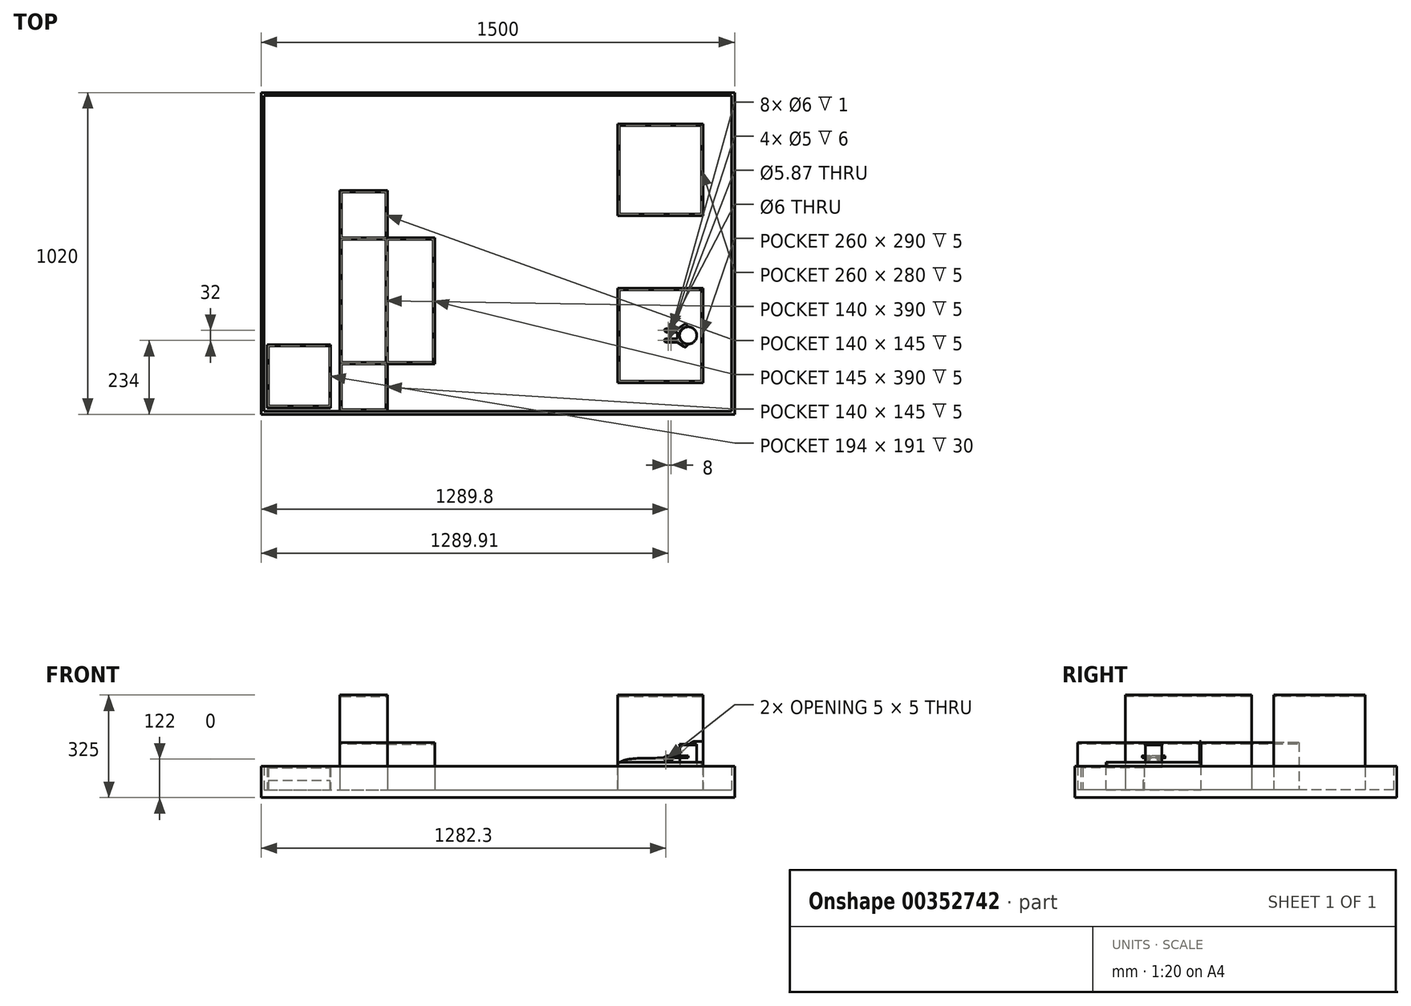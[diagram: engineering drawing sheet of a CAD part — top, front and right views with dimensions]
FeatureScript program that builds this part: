
annotation { "Feature Type Name" : "Feature", "Feature Type Description" : "" }
export const myFeature = defineFeature(function(context is Context, id is Id, definition is map)
    precondition{}
    {
        {
            var Q0;
            Q0=qCreatedBy(makeId("Top.planeOp"),FACE);
            var sketch = newSketch(context, id + "F0", { "sketchPlane" : qUnion([Q0])});
            skCircle(sketch, "E0", {"center": v(0, 0) * mm, "radius": 27.2 * mm});
            skSolve(sketch);
        }
        {
            var Q0;
            Q0=qSketchRegion(id+"F0",true);
            extrude(context, id + "F1", {"entities" : qUnion([Q0]), "depth" : 2.83 * mm});
        }
        {
            var Q0;
            Q0=makeQuery(id+"F1.opExtrude","CAP_FACE",FACE,{"disambiguationData":[OSD([sQuery(id+"F0.wireOp",EDGE,"E0")])],"isStart":false});
            var sketch = newSketch(context, id + "F2", { "sketchPlane" : qUnion([Q0])});
            skCircle(sketch, "E1", {"center": v(0, 0) * mm, "radius": 26.4 * mm});
            skSolve(sketch);
        }
        {
            var Q0;
            Q0=qSketchRegion(id+"F2",true);
            extrude(context, id + "F3", {"entities" : qUnion([Q0]), "operationType" : NewBodyOperationType.ADD, "depth" : 67.36 * mm});
        }
        {
            var Q0;
            Q0=makeQuery(id+"F3.opExtrude","CAP_FACE",FACE,{"disambiguationData":[OSD([sQuery(id+"F2.wireOp",EDGE,"E1")])],"isStart":false});
            var sketch = newSketch(context, id + "F4", { "sketchPlane" : qUnion([Q0])});
            skCircle(sketch, "E2", {"center": v(0, 0) * mm, "radius": 27.2 * mm});
            skSolve(sketch);
        }
        {
            var Q0;
            Q0=qSketchRegion(id+"F4",true);
            extrude(context, id + "F5", {"entities" : qUnion([Q0]), "operationType" : NewBodyOperationType.ADD, "depth" : 2.83 * mm});
        }
        {
            var Q0;
            Q0=makeQuery(id+"F5.opExtrude","CAP_FACE",FACE,{"disambiguationData":[OSD([sQuery(id+"F4.wireOp",EDGE,"E2")])],"isStart":false});
            var sketch = newSketch(context, id + "F6", { "sketchPlane" : qUnion([Q0])});
            skSolve(sketch);
        }
        {
            var Q0;
            Q0=qCreatedBy(makeId("Top.planeOp"),FACE);
            cPlane(context, id + "F7", {"entities" : qUnion([Q0]), "cplaneType" : CPlaneType.OFFSET, "offset" : 25 * mm, "width" : 150 * mm, "height" : 150 * mm});
        }
        {
            var Q0;
            Q0=makeQuery(id+"F6.imprint","IMPRINT",FACE,{"disambiguationData":[TD([[makeQuery(id+"F6.imprint","IMPRINT",EDGE,{"derivedFrom":makeQuery(id+"F5.opExtrude","CAP_EDGE",EDGE,{"disambiguationData":[OSD([sQuery(id+"F4.wireOp",EDGE,"E2")])],"isStart":false})}),1.0]])]});
            var sketch = newSketch(context, id + "F8", { "sketchPlane" : qUnion([Q0])});
            skSolve(sketch);
        }
        {
            var Q0;
            Q0=qCreatedBy(makeId("Top.planeOp"),FACE);
            var sketch = newSketch(context, id + "F9", { "sketchPlane" : qUnion([Q0])});
            skLineSegment(sketch, "E3.bottom", {"start": v(-222.8, -150) * mm, "end": v(47.2, -150) * mm});
            skLineSegment(sketch, "E3.top", {"start": v(-222.8, 150) * mm, "end": v(47.2, 150) * mm});
            skLineSegment(sketch, "E3.left", {"start": v(-222.8, -150) * mm, "end": v(-222.8, 150) * mm});
            skLineSegment(sketch, "E3.right", {"start": v(47.2, -150) * mm, "end": v(47.2, 150) * mm});
            skSolve(sketch);
        }
        {
            var Q0;
            Q0=qSketchRegion(id+"F9",true);
            extrude(context, id + "F10", {"entities" : qUnion([Q0]), "oppositeDirection" : true, "depth" : 72 * mm});
        }
        {
            var Q0;
            Q0=makeQuery(id+"F10.opExtrude","CAP_FACE",FACE,{"disambiguationData":[OSD([sQuery(id+"F9.wireOp",EDGE,"E3.bottom"),sQuery(id+"F9.wireOp",EDGE,"E3.top"),sQuery(id+"F9.wireOp",EDGE,"E3.left"),sQuery(id+"F9.wireOp",EDGE,"E3.right")])],"isStart":true});
            var sketch = newSketch(context, id + "F11", { "sketchPlane" : qUnion([Q0])});
            skLineSegment(sketch, "E4.bottom", {"start": v(-222.8, -150) * mm, "end": v(47.2, -150) * mm});
            skLineSegment(sketch, "E4.top", {"start": v(-222.8, -145) * mm, "end": v(42.2, -145) * mm});
            skLineSegment(sketch, "E4.left", {"start": v(-222.8, -150) * mm, "end": v(-222.8, -145) * mm});
            skLineSegment(sketch, "E5.bottom", {"start": v(47.2, 150) * mm, "end": v(42.2, 150) * mm});
            skLineSegment(sketch, "E5.left", {"start": v(47.2, 150) * mm, "end": v(47.2, -150) * mm});
            skLineSegment(sketch, "E5.right", {"start": v(42.2, 150) * mm, "end": v(42.2, -145) * mm});
            skSolve(sketch);
        }
        {
            var Q0;
            Q0=qSketchRegion(id+"F11",true);
            extrude(context, id + "F12", {"entities" : qUnion([Q0]), "operationType" : NewBodyOperationType.ADD, "depth" : 15 * mm});
        }
        {
            var Q0;
            Q0=makeQuery(id+"F12.boolean.opBoolean","MERGE",FACE,{"derivedFrom":[makeQuery(id+"F10.opExtrude","SWEPT_FACE",FACE,{"disambiguationData":[OSD([sQuery(id+"F9.wireOp",EDGE,"E3.top")])]}),makeQuery(id+"F12.opExtrude","SWEPT_FACE",FACE,{"disambiguationData":[OSD([sQuery(id+"F11.wireOp",EDGE,"E5.bottom")])]})]});
            var sketch = newSketch(context, id + "F13", { "sketchPlane" : qUnion([Q0])});
            skLineSegment(sketch, "E6", {"start": v(-47.2, 81.36) * mm, "end": v(-21.31, 81.36) * mm});
            skFitSpline(sketch, "E7", {"points": [v(-21.31, 81.36) * mm, v(15.24, 52.01) * mm, v(114.14, 28.17) * mm, v(222.8, 0) * mm], "startDerivative": vector(181.02, 0.3) * mm, "endDerivative": vector(-1.73, -239.85) * mm});
            skLineSegment(sketch, "E8", {"start": v(-47.2, 81.36) * mm, "end": v(-47.2, -72) * mm});
            skLineSegment(sketch, "E9", {"start": v(-47.2, -72) * mm, "end": v(222.8, -72) * mm});
            skLineSegment(sketch, "E10", {"start": v(222.8, -72) * mm, "end": v(222.8, 0) * mm});
            skSolve(sketch);
        }
        {
            var Q0;
            Q0=qSketchRegion(id+"F13",true);
            extrude(context, id + "F14", {"entities" : qUnion([Q0]), "operationType" : NewBodyOperationType.ADD, "oppositeDirection" : true, "depth" : 5 * mm});
        }
        {
            var Q0;
            Q0=makeQuery(id+"F10.opExtrude","CAP_FACE",FACE,{"disambiguationData":[OSD([sQuery(id+"F9.wireOp",EDGE,"E3.bottom"),sQuery(id+"F9.wireOp",EDGE,"E3.top"),sQuery(id+"F9.wireOp",EDGE,"E3.left"),sQuery(id+"F9.wireOp",EDGE,"E3.right")])],"isStart":true});
            var sketch = newSketch(context, id + "F15", { "sketchPlane" : qUnion([Q0])});
            skLineSegment(sketch, "E11.bottom", {"start": v(-222.8, 145) * mm, "end": v(-217.8, 145) * mm});
            skLineSegment(sketch, "E11.top", {"start": v(-222.8, -145) * mm, "end": v(-217.8, -145) * mm});
            skLineSegment(sketch, "E11.left", {"start": v(-222.8, 145) * mm, "end": v(-222.8, -145) * mm});
            skLineSegment(sketch, "E11.right", {"start": v(-217.8, 145) * mm, "end": v(-217.8, -145) * mm});
            skSolve(sketch);
        }
        {
            var Q0;
            Q0=qSketchRegion(id+"F15",true);
            extrude(context, id + "F16", {"entities" : qUnion([Q0]), "operationType" : NewBodyOperationType.ADD, "depth" : 5 * mm});
        }
        {
            var Q0;
            Q0=makeQuery(id+"F10.opExtrude","CAP_FACE",FACE,{"disambiguationData":[OSD([sQuery(id+"F9.wireOp",EDGE,"E3.bottom"),sQuery(id+"F9.wireOp",EDGE,"E3.top"),sQuery(id+"F9.wireOp",EDGE,"E3.left"),sQuery(id+"F9.wireOp",EDGE,"E3.right")])],"isStart":false});
            var sketch = newSketch(context, id + "F17", { "sketchPlane" : qUnion([Q0])});
            skLineSegment(sketch, "E12.bottom", {"start": v(147.2, 250) * mm, "end": v(-1352.8, 250) * mm});
            skLineSegment(sketch, "E12.top", {"start": v(147.2, -770) * mm, "end": v(-1352.8, -770) * mm});
            skLineSegment(sketch, "E12.left", {"start": v(147.2, 250) * mm, "end": v(147.2, -770) * mm});
            skLineSegment(sketch, "E12.right", {"start": v(-1352.8, 250) * mm, "end": v(-1352.8, -770) * mm});
            skSolve(sketch);
        }
        {
            var Q0;
            Q0=qSketchRegion(id+"F17",true);
            extrude(context, id + "F18", {"entities" : qUnion([Q0]), "operationType" : NewBodyOperationType.ADD, "depth" : 25 * mm});
        }
        {
            var Q0;
            Q0=makeQuery(id+"F18.opExtrude","CAP_FACE",FACE,{"disambiguationData":[OSD([sQuery(id+"F17.wireOp",EDGE,"E12.bottom"),sQuery(id+"F17.wireOp",EDGE,"E12.top"),sQuery(id+"F17.wireOp",EDGE,"E12.left"),sQuery(id+"F17.wireOp",EDGE,"E12.right")])],"isStart":true});
            var sketch = newSketch(context, id + "F19", { "sketchPlane" : qUnion([Q0])});
            skLineSegment(sketch, "E13.bottom", {"start": v(-222.8, 670) * mm, "end": v(47.2, 670) * mm});
            skLineSegment(sketch, "E13.top", {"start": v(-222.8, 380) * mm, "end": v(47.2, 380) * mm});
            skLineSegment(sketch, "E13.left", {"start": v(-222.8, 670) * mm, "end": v(-222.8, 380) * mm});
            skLineSegment(sketch, "E13.right", {"start": v(47.2, 670) * mm, "end": v(47.2, 380) * mm});
            skSolve(sketch);
        }
        {
            var Q0;
            Q0=qSketchRegion(id+"F19",true);
            extrude(context, id + "F20", {"entities" : qUnion([Q0]), "operationType" : NewBodyOperationType.ADD, "depth" : 300 * mm});
        }
        {
            var Q0;
            Q0=makeQuery(id+"F20.opExtrude","CAP_FACE",FACE,{"disambiguationData":[OSD([sQuery(id+"F19.wireOp",EDGE,"E13.bottom"),sQuery(id+"F19.wireOp",EDGE,"E13.top"),sQuery(id+"F19.wireOp",EDGE,"E13.left"),sQuery(id+"F19.wireOp",EDGE,"E13.right")])],"isStart":false});
            var sketch = newSketch(context, id + "F21", { "sketchPlane" : qUnion([Q0])});
            skLineSegment(sketch, "E14.bottom", {"start": v(-217.8, 665) * mm, "end": v(42.2, 665) * mm});
            skLineSegment(sketch, "E14.top", {"start": v(-217.8, 385) * mm, "end": v(42.2, 385) * mm});
            skLineSegment(sketch, "E14.left", {"start": v(-217.8, 665) * mm, "end": v(-217.8, 385) * mm});
            skLineSegment(sketch, "E14.right", {"start": v(42.2, 665) * mm, "end": v(42.2, 385) * mm});
            skSolve(sketch);
        }
        {
            var Q0;
            Q0=qSketchRegion(id+"F21",true);
            extrude(context, id + "F22", {"entities" : qUnion([Q0]), "operationType" : NewBodyOperationType.REMOVE, "oppositeDirection" : true, "depth" : 5 * mm});
        }
        {
            var Q0;
            Q0=makeQuery(id+"F18.opExtrude","CAP_FACE",FACE,{"disambiguationData":[OSD([sQuery(id+"F17.wireOp",EDGE,"E12.bottom"),sQuery(id+"F17.wireOp",EDGE,"E12.top"),sQuery(id+"F17.wireOp",EDGE,"E12.left"),sQuery(id+"F17.wireOp",EDGE,"E12.right")])],"isStart":true});
            var sketch = newSketch(context, id + "F23", { "sketchPlane" : qUnion([Q0])});
            skLineSegment(sketch, "E15.bottom", {"start": v(-1352.8, 770) * mm, "end": v(147.2, 770) * mm});
            skLineSegment(sketch, "E15.top", {"start": v(-1352.8, -250) * mm, "end": v(147.2, -250) * mm});
            skLineSegment(sketch, "E15.left", {"start": v(-1352.8, 770) * mm, "end": v(-1352.8, -250) * mm});
            skLineSegment(sketch, "E15.right", {"start": v(147.2, 770) * mm, "end": v(147.2, -250) * mm});
            skLineSegment(sketch, "E16.bottom", {"start": v(-1342.8, 760) * mm, "end": v(137.2, 760) * mm});
            skLineSegment(sketch, "E16.top", {"start": v(-1342.8, -240) * mm, "end": v(137.2, -240) * mm});
            skLineSegment(sketch, "E16.left", {"start": v(-1342.8, 760) * mm, "end": v(-1342.8, -240) * mm});
            skLineSegment(sketch, "E16.right", {"start": v(137.2, 760) * mm, "end": v(137.2, -240) * mm});
            skSolve(sketch);
        }
        {
            var Q0;
            Q0=qSketchRegion(id+"F23",true);
            extrude(context, id + "F24", {"entities" : qUnion([Q0]), "operationType" : NewBodyOperationType.ADD, "depth" : 75 * mm});
        }
        {
            var Q0;
            Q0=makeQuery(id+"F18.opExtrude","CAP_FACE",FACE,{"disambiguationData":[OSD([sQuery(id+"F17.wireOp",EDGE,"E12.bottom"),sQuery(id+"F17.wireOp",EDGE,"E12.top"),sQuery(id+"F17.wireOp",EDGE,"E12.left"),sQuery(id+"F17.wireOp",EDGE,"E12.right")])],"isStart":true});
            var sketch = newSketch(context, id + "F25", { "sketchPlane" : qUnion([Q0])});
            skLineSegment(sketch, "E17.bottom", {"start": v(-1102.8, 460) * mm, "end": v(-952.8, 460) * mm});
            skLineSegment(sketch, "E17.top", {"start": v(-1102.8, -240) * mm, "end": v(-952.8, -240) * mm});
            skLineSegment(sketch, "E17.left", {"start": v(-1102.8, 460) * mm, "end": v(-1102.8, -240) * mm});
            skLineSegment(sketch, "E17.right", {"start": v(-952.8, 460) * mm, "end": v(-952.8, 310) * mm});
            skLineSegment(sketch, "E18.bottom", {"start": v(-952.8, 310) * mm, "end": v(-802.8, 310) * mm});
            skLineSegment(sketch, "E18.top", {"start": v(-952.8, -90) * mm, "end": v(-802.8, -90) * mm});
            skLineSegment(sketch, "E18.right", {"start": v(-802.8, 310) * mm, "end": v(-802.8, -90) * mm});
            skLineSegment(sketch, "E19.trimOffspring", {"start": v(-952.8, -90) * mm, "end": v(-952.8, -240) * mm});
            skSolve(sketch);
        }
        {
            var Q0;
            Q0=qSketchRegion(id+"F25",true);
            extrude(context, id + "F26", {"entities" : qUnion([Q0]), "operationType" : NewBodyOperationType.ADD, "depth" : 150 * mm});
        }
        {
            var Q0;
            Q0=makeQuery(id+"F26.opExtrude","CAP_FACE",FACE,{"disambiguationData":[OSD([sQuery(id+"F25.wireOp",EDGE,"E17.bottom"),sQuery(id+"F25.wireOp",EDGE,"E17.top"),sQuery(id+"F25.wireOp",EDGE,"E17.left"),sQuery(id+"F25.wireOp",EDGE,"E17.right"),sQuery(id+"F25.wireOp",EDGE,"E18.bottom"),sQuery(id+"F25.wireOp",EDGE,"E18.top"),sQuery(id+"F25.wireOp",EDGE,"E18.right"),sQuery(id+"F25.wireOp",EDGE,"E19.trimOffspring")])],"isStart":false});
            var sketch = newSketch(context, id + "F27", { "sketchPlane" : qUnion([Q0])});
            skLineSegment(sketch, "E20.bottom", {"start": v(-952.8, 310) * mm, "end": v(-1102.8, 310) * mm});
            skLineSegment(sketch, "E20.top", {"start": v(-952.8, -90) * mm, "end": v(-1102.8, -90) * mm});
            skLineSegment(sketch, "E20.left", {"start": v(-952.8, 310) * mm, "end": v(-952.8, -90) * mm});
            skLineSegment(sketch, "E20.right", {"start": v(-1102.8, 310) * mm, "end": v(-1102.8, -90) * mm});
            skSolve(sketch);
        }
        {
            var Q0;
            Q0=qSketchRegion(id+"F27",true);
            extrude(context, id + "F28", {"entities" : qUnion([Q0]), "operationType" : NewBodyOperationType.ADD, "depth" : 150 * mm});
        }
        {
            var Q0;
            Q0=makeQuery(id+"F28.opExtrude","CAP_FACE",FACE,{"disambiguationData":[OSD([sQuery(id+"F27.wireOp",EDGE,"E20.bottom"),sQuery(id+"F27.wireOp",EDGE,"E20.top"),sQuery(id+"F27.wireOp",EDGE,"E20.left"),sQuery(id+"F27.wireOp",EDGE,"E20.right")])],"isStart":false});
            var sketch = newSketch(context, id + "F29", { "sketchPlane" : qUnion([Q0])});
            skLineSegment(sketch, "E21.bottom", {"start": v(-1097.8, 305) * mm, "end": v(-957.8, 305) * mm});
            skLineSegment(sketch, "E21.top", {"start": v(-1097.8, -85) * mm, "end": v(-957.8, -85) * mm});
            skLineSegment(sketch, "E21.left", {"start": v(-1097.8, 305) * mm, "end": v(-1097.8, -85) * mm});
            skLineSegment(sketch, "E21.right", {"start": v(-957.8, 305) * mm, "end": v(-957.8, -85) * mm});
            skSolve(sketch);
        }
        {
            var Q0;
            Q0=qSketchRegion(id+"F29",true);
            extrude(context, id + "F30", {"entities" : qUnion([Q0]), "operationType" : NewBodyOperationType.REMOVE, "oppositeDirection" : true, "depth" : 5 * mm});
        }
        {
            var Q0;
            {var subQ0=sQuery(id+"F25.wireOp",EDGE,"E17.left");var subQ1=sQuery(id+"F25.wireOp",EDGE,"E18.bottom");var subQ2=sQuery(id+"F25.wireOp",EDGE,"E17.right");var subQ3=sQuery(id+"F25.wireOp",EDGE,"E17.bottom");var subQ4=makeQuery(id+"F26.opExtrude","CAP_FACE",FACE,{"disambiguationData":[OSD([subQ3,sQuery(id+"F25.wireOp",EDGE,"E17.top"),subQ0,subQ2,subQ1,sQuery(id+"F25.wireOp",EDGE,"E18.top"),sQuery(id+"F25.wireOp",EDGE,"E18.right"),sQuery(id+"F25.wireOp",EDGE,"E19.trimOffspring")])],"isStart":false});Q0=makeQuery(id+"F28.boolean.opBoolean","SPLIT",FACE,{"disambiguationData":[TD([makeQuery(id+"F26.opExtrude","SWEPT_FACE",FACE,{"disambiguationData":[OSD([subQ3])]})])],"derivedFrom":subQ4});}
            var sketch = newSketch(context, id + "F31", { "sketchPlane" : qUnion([Q0])});
            skLineSegment(sketch, "E22.bottom", {"start": v(-1097.8, 455) * mm, "end": v(-957.8, 455) * mm});
            skLineSegment(sketch, "E22.top", {"start": v(-1097.8, 310) * mm, "end": v(-957.8, 310) * mm});
            skLineSegment(sketch, "E22.left", {"start": v(-1097.8, 455) * mm, "end": v(-1097.8, 310) * mm});
            skLineSegment(sketch, "E22.right", {"start": v(-957.8, 455) * mm, "end": v(-957.8, 310) * mm});
            skLineSegment(sketch, "E23.bottom", {"start": v(-952.8, 305) * mm, "end": v(-807.8, 305) * mm});
            skLineSegment(sketch, "E23.top", {"start": v(-952.8, -85) * mm, "end": v(-807.8, -85) * mm});
            skLineSegment(sketch, "E23.left", {"start": v(-952.8, 305) * mm, "end": v(-952.8, -85) * mm});
            skLineSegment(sketch, "E23.right", {"start": v(-807.8, 305) * mm, "end": v(-807.8, -85) * mm});
            skLineSegment(sketch, "E24.bottom", {"start": v(-1097.8, -90) * mm, "end": v(-957.8, -90) * mm});
            skLineSegment(sketch, "E24.top", {"start": v(-1097.8, -235) * mm, "end": v(-957.8, -235) * mm});
            skLineSegment(sketch, "E24.left", {"start": v(-1097.8, -90) * mm, "end": v(-1097.8, -235) * mm});
            skLineSegment(sketch, "E24.right", {"start": v(-957.8, -90) * mm, "end": v(-957.8, -235) * mm});
            skSolve(sketch);
        }
        {
            var Q0;
            Q0=qSketchRegion(id+"F31",true);
            extrude(context, id + "F32", {"entities" : qUnion([Q0]), "operationType" : NewBodyOperationType.REMOVE, "oppositeDirection" : true, "depth" : 5 * mm});
        }
        {
            var Q0;
            Q0=qCreatedBy(id+"F7.planeOp",FACE);
            var sketch = newSketch(context, id + "F33", { "sketchPlane" : qUnion([Q0])});
            skLineSegment(sketch, "E25", {"start": v(0, 0) * mm, "end": v(-90, 0) * mm, "construction": true});
            skLineSegment(sketch, "E26.bottom", {"start": v(-74.5, -12) * mm, "end": v(-55, -12) * mm});
            skLineSegment(sketch, "E26.top", {"start": v(-74.5, -20) * mm, "end": v(-55, -20) * mm});
            skLineSegment(sketch, "E26.left", {"start": v(-74.5, -12) * mm, "end": v(-74.5, -13) * mm});
            skPoint(sketch, "E27.visualSharp", {"position": v(-51, -12) * mm});
            skPoint(sketch, "E28.visualSharp", {"position": v(-51, -20) * mm});
            skCircle(sketch, "E29", {"center": v(-55, -16) * mm, "radius": 3 * mm});
            skLineSegment(sketch, "E30", {"start": v(-59, -3.98) * mm, "end": v(-59, -18.08) * mm, "construction": true});
            skCircle(sketch, "E31.MirrorC", {"center": v(-63, -16) * mm, "radius": 3 * mm});
            skLineSegment(sketch, "E32.bottom", {"start": v(-74.5, -13) * mm, "end": v(-65.65, -13) * mm});
            skLineSegment(sketch, "E32.top", {"start": v(-74.5, -19) * mm, "end": v(-65.65, -19) * mm});
            skArc(sketch, "E33", {"start": v(-65.65, -13) * mm, "mid": v(-67, -16) * mm, "end": v(-65.65, -19) * mm});
            skLineSegment(sketch, "E34.trimOffspring", {"start": v(-74.5, -19) * mm, "end": v(-74.5, -20) * mm});
            skArc(sketch, "E35.trimOffspring", {"start": v(-55, -20) * mm, "mid": v(-51, -16) * mm, "end": v(-55, -12) * mm});
            skLineSegment(sketch, "E36.MirrorCS", {"start": v(-74.5, 12) * mm, "end": v(-74.5, 13) * mm});
            skLineSegment(sketch, "E37.MirrorCS", {"start": v(-74.5, 19) * mm, "end": v(-74.5, 20) * mm});
            skPoint(sketch, "E38.MirrorP", {"position": v(-51, 12) * mm});
            skLineSegment(sketch, "E39.MirrorCS", {"start": v(-74.5, 12) * mm, "end": v(-55, 12) * mm});
            skPoint(sketch, "E40.MirrorP", {"position": v(-51, 20) * mm});
            skArc(sketch, "E41.MirrorCS", {"start": v(-65.65, 13) * mm, "mid": v(-67, 16) * mm, "end": v(-65.65, 19) * mm});
            skArc(sketch, "E42.MirrorCS", {"start": v(-55, 20) * mm, "mid": v(-51, 16) * mm, "end": v(-55, 12) * mm});
            skLineSegment(sketch, "E43.MirrorCS", {"start": v(-74.5, 20) * mm, "end": v(-55, 20) * mm});
            skCircle(sketch, "E44.MirrorC", {"center": v(-55, 16) * mm, "radius": 3 * mm});
            skCircle(sketch, "E45.MirrorC", {"center": v(-63, 16) * mm, "radius": 3 * mm});
            skLineSegment(sketch, "E46.MirrorCS", {"start": v(-74.5, 19) * mm, "end": v(-65.65, 19) * mm});
            skLineSegment(sketch, "E47.MirrorCS", {"start": v(-74.5, 13) * mm, "end": v(-65.65, 13) * mm});
            skSolve(sketch);
        }
        {
            var Q0;
            Q0=qSketchRegion(id+"F33",true);
            var Q1;
            Q1=qSketchRegion(id+"F36",true);
            extrude(context, id + "F34", {"entities" : qUnion([Q0, Q1]), "endBound" : BoundingType.SYMMETRIC, "depth" : 8 * mm});
        }
        {
            var Q0;
            Q0=makeQuery(id+"F34.opExtrude","CAP_EDGE",EDGE,{"disambiguationData":[OSD([sQuery(id+"F33.wireOp",EDGE,"E34.trimOffspring")])],"isStart":false});
            var Q1;
            Q1=makeQuery(id+"F34.opExtrude","CAP_EDGE",EDGE,{"disambiguationData":[OSD([sQuery(id+"F33.wireOp",EDGE,"E26.left")])],"isStart":false});
            var Q2;
            Q2=makeQuery(id+"F34.opExtrude","CAP_EDGE",EDGE,{"disambiguationData":[OSD([sQuery(id+"F33.wireOp",EDGE,"E34.trimOffspring")])],"isStart":true});
            var Q3;
            Q3=makeQuery(id+"F34.opExtrude","CAP_EDGE",EDGE,{"disambiguationData":[OSD([sQuery(id+"F33.wireOp",EDGE,"E26.left")])],"isStart":true});
            var Q4;
            Q4=makeQuery(id+"F34.opExtrude","CAP_EDGE",EDGE,{"disambiguationData":[OSD([sQuery(id+"F33.wireOp",EDGE,"E36.MirrorCS")])],"isStart":false});
            var Q5;
            Q5=makeQuery(id+"F34.opExtrude","CAP_EDGE",EDGE,{"disambiguationData":[OSD([sQuery(id+"F33.wireOp",EDGE,"E37.MirrorCS")])],"isStart":false});
            var Q6;
            Q6=makeQuery(id+"F34.opExtrude","CAP_EDGE",EDGE,{"disambiguationData":[OSD([sQuery(id+"F33.wireOp",EDGE,"E37.MirrorCS")])],"isStart":true});
            var Q7;
            Q7=makeQuery(id+"F34.opExtrude","CAP_EDGE",EDGE,{"disambiguationData":[OSD([sQuery(id+"F33.wireOp",EDGE,"E36.MirrorCS")])],"isStart":true});
            fillet(context, id + "F35", {"entities" : qUnion([Q0, Q1, Q2, Q3, Q4, Q5, Q6, Q7]), "radius" : 4 * mm, "tangentPropagation" : true, "allowEdgeOverflow" : false});
        }
        {
            var Q0;
            Q0=makeQuery(id+"F34.opExtrude","SWEPT_FACE",FACE,{"disambiguationData":[OSD([sQuery(id+"F33.wireOp",EDGE,"E26.top")])]});
            var sketch = newSketch(context, id + "F36", { "sketchPlane" : qUnion([Q0])});
            skCircle(sketch, "E48", {"center": v(-70.5, 25) * mm, "radius": 3 * mm});
            skSolve(sketch);
        }
        {
            var Q0;
            Q0=qSketchRegion(id+"F36",true);
            var Q1;
            Q1=makeQuery(id+"F34.opExtrude","SWEPT_FACE",FACE,{"disambiguationData":[OSD([sQuery(id+"F33.wireOp",EDGE,"E26.bottom")])]});
            extrude(context, id + "F37", {"entities" : qUnion([Q0]), "operationType" : NewBodyOperationType.ADD, "endBound" : BoundingType.UP_TO_SURFACE, "oppositeDirection" : true, "endBoundEntityFace" : qUnion([Q1]), "depth" : 25 * mm});
        }
        {
            var Q0;
            Q0=makeQuery(id+"F34.opExtrude","SWEPT_FACE",FACE,{"disambiguationData":[OSD([sQuery(id+"F33.wireOp",EDGE,"E43.MirrorCS")])]});
            var sketch = newSketch(context, id + "F38", { "sketchPlane" : qUnion([Q0])});
            skCircle(sketch, "E49", {"center": v(70.5, 25) * mm, "radius": 3 * mm});
            skSolve(sketch);
        }
        {
            var Q0;
            Q0=qSketchRegion(id+"F38",true);
            var Q1;
            Q1=makeQuery(id+"F34.opExtrude","SWEPT_FACE",FACE,{"disambiguationData":[OSD([sQuery(id+"F33.wireOp",EDGE,"E39.MirrorCS")])]});
            extrude(context, id + "F39", {"entities" : qUnion([Q0]), "operationType" : NewBodyOperationType.ADD, "endBound" : BoundingType.UP_TO_SURFACE, "oppositeDirection" : true, "endBoundEntityFace" : qUnion([Q1]), "depth" : 25 * mm});
        }
        {
            var Q0;
            Q0=qCreatedBy(id+"F7.planeOp",FACE);
            var sketch = newSketch(context, id + "F40", { "sketchPlane" : qUnion([Q0])});
            skCircle(sketch, "E50", {"center": v(-55, 16) * mm, "radius": 3 * mm});
            skCircle(sketch, "E51", {"center": v(-63, 16) * mm, "radius": 2.5 * mm});
            skCircle(sketch, "E52", {"center": v(-63, 16) * mm, "radius": 3 * mm});
            skCircle(sketch, "E53", {"center": v(-55, 16) * mm, "radius": 2.5 * mm});
            skSolve(sketch);
        }
        {
            var Q0;
            Q0=qSketchRegion(id+"F40",true);
            extrude(context, id + "F41", {"entities" : qUnion([Q0]), "operationType" : NewBodyOperationType.ADD, "endBound" : BoundingType.SYMMETRIC, "depth" : 6 * mm});
        }
        {
            var Q0;
            Q0=qCreatedBy(id+"F7.planeOp",FACE);
            var sketch = newSketch(context, id + "F42", { "sketchPlane" : qUnion([Q0])});
            skCircle(sketch, "E54", {"center": v(-63, -16) * mm, "radius": 2.5 * mm});
            skCircle(sketch, "E55", {"center": v(-63, -16) * mm, "radius": 3 * mm});
            skCircle(sketch, "E56", {"center": v(-55, -16) * mm, "radius": 2.5 * mm});
            skCircle(sketch, "E57", {"center": v(-55, -16) * mm, "radius": 3 * mm});
            skSolve(sketch);
        }
        {
            var Q0;
            Q0=qSketchRegion(id+"F42",true);
            extrude(context, id + "F43", {"entities" : qUnion([Q0]), "operationType" : NewBodyOperationType.ADD, "endBound" : BoundingType.SYMMETRIC, "depth" : 6 * mm});
        }
        {
            var Q0;
            Q0=makeQuery(id+"F34.opExtrude","SWEPT_FACE",FACE,{"disambiguationData":[OSD([sQuery(id+"F33.wireOp",EDGE,"E43.MirrorCS")])]});
            var sketch = newSketch(context, id + "F44", { "sketchPlane" : qUnion([Q0])});
            skArc(sketch, "E58", {"start": v(71.5, 27.3) * mm, "mid": v(70.5, 27.5) * mm, "end": v(69.5, 27.3) * mm});
            skLineSegment(sketch, "E59.bottom", {"start": v(68.2, 26) * mm, "end": v(69.5, 26) * mm});
            skLineSegment(sketch, "E59.top", {"start": v(68.2, 24) * mm, "end": v(69.5, 24) * mm});
            skLineSegment(sketch, "E60.left", {"start": v(71.5, 27.3) * mm, "end": v(71.5, 26) * mm});
            skLineSegment(sketch, "E60.right", {"start": v(69.5, 27.3) * mm, "end": v(69.5, 26) * mm});
            skPoint(sketch, "E61.orphan", {"position": v(69.5, 27.8) * mm});
            skPoint(sketch, "E62.orphan", {"position": v(71.5, 27.8) * mm});
            skArc(sketch, "E63.trimOffspring", {"start": v(68.2, 26) * mm, "mid": v(68, 25) * mm, "end": v(68.2, 24) * mm});
            skPoint(sketch, "E59.left.start.orphan", {"position": v(67.32, 26) * mm});
            skPoint(sketch, "E64.orphan", {"position": v(67.32, 24) * mm});
            skArc(sketch, "E65.trimOffspring", {"start": v(69.5, 22.7) * mm, "mid": v(70.5, 22.5) * mm, "end": v(71.5, 22.7) * mm});
            skLineSegment(sketch, "E66.trimOffspring", {"start": v(69.5, 24) * mm, "end": v(69.5, 22.7) * mm});
            skLineSegment(sketch, "E67.trimOffspring", {"start": v(71.5, 26) * mm, "end": v(72.8, 26) * mm});
            skLineSegment(sketch, "E68.trimOffspring", {"start": v(71.5, 24) * mm, "end": v(71.5, 22.7) * mm});
            skLineSegment(sketch, "E69.trimOffspring", {"start": v(71.5, 24) * mm, "end": v(72.8, 24) * mm});
            skPoint(sketch, "E60.top.end.orphan", {"position": v(69.5, 22.2) * mm});
            skPoint(sketch, "E70.orphan", {"position": v(71.5, 22.2) * mm});
            skPoint(sketch, "E59.right.end.orphan", {"position": v(73.68, 24) * mm});
            skPoint(sketch, "E71.orphan", {"position": v(73.68, 26) * mm});
            skArc(sketch, "E72.trimOffspring", {"start": v(72.8, 24) * mm, "mid": v(73, 25) * mm, "end": v(72.8, 26) * mm});
            skSolve(sketch);
        }
        {
            var Q0;
            Q0=qSketchRegion(id+"F44",true);
            extrude(context, id + "F45", {"entities" : qUnion([Q0]), "operationType" : NewBodyOperationType.REMOVE, "endBound" : BoundingType.THROUGH_ALL, "oppositeDirection" : true, "depth" : 25 * mm});
        }
        {
            var Q0;
            Q0=makeQuery(id+"F18.opExtrude","CAP_FACE",FACE,{"disambiguationData":[OSD([sQuery(id+"F17.wireOp",EDGE,"E12.bottom"),sQuery(id+"F17.wireOp",EDGE,"E12.top"),sQuery(id+"F17.wireOp",EDGE,"E12.left"),sQuery(id+"F17.wireOp",EDGE,"E12.right")])],"isStart":true});
            var sketch = newSketch(context, id + "F46", { "sketchPlane" : qUnion([Q0])});
            skLineSegment(sketch, "E73.bottom", {"start": v(-1332.8, -30) * mm, "end": v(-1132.8, -30) * mm});
            skLineSegment(sketch, "E73.top", {"start": v(-1332.8, -230) * mm, "end": v(-1132.8, -230) * mm});
            skLineSegment(sketch, "E73.left", {"start": v(-1332.8, -30) * mm, "end": v(-1332.8, -230) * mm});
            skLineSegment(sketch, "E73.right", {"start": v(-1132.8, -30) * mm, "end": v(-1132.8, -230) * mm});
            skLineSegment(sketch, "E74.bottom", {"start": v(-1329.8, -33) * mm, "end": v(-1135.8, -33) * mm});
            skLineSegment(sketch, "E74.top", {"start": v(-1329.8, -224) * mm, "end": v(-1135.8, -224) * mm});
            skLineSegment(sketch, "E74.left", {"start": v(-1329.8, -33) * mm, "end": v(-1329.8, -224) * mm});
            skLineSegment(sketch, "E74.right", {"start": v(-1135.8, -33) * mm, "end": v(-1135.8, -224) * mm});
            skSolve(sketch);
        }
        {
            var Q0;
            Q0=qSketchRegion(id+"F46",true);
            extrude(context, id + "F47", {"entities" : qUnion([Q0]), "operationType" : NewBodyOperationType.ADD, "depth" : 30 * mm});
        }
        {
            var Q0;
            Q0=makeQuery(id+"F47.opExtrude","CAP_FACE",FACE,{"disambiguationData":[OSD([sQuery(id+"F46.wireOp",EDGE,"E73.bottom"),sQuery(id+"F46.wireOp",EDGE,"E73.top"),sQuery(id+"F46.wireOp",EDGE,"E73.left"),sQuery(id+"F46.wireOp",EDGE,"E73.right"),sQuery(id+"F46.wireOp",EDGE,"E74.bottom"),sQuery(id+"F46.wireOp",EDGE,"E74.top"),sQuery(id+"F46.wireOp",EDGE,"E74.left"),sQuery(id+"F46.wireOp",EDGE,"E74.right")])],"isStart":false});
            var sketch = newSketch(context, id + "F48", { "sketchPlane" : qUnion([Q0])});
            skLineSegment(sketch, "E75.bottom", {"start": v(-1332.8, -30) * mm, "end": v(-1329.8, -30) * mm});
            skLineSegment(sketch, "E75.top", {"start": v(-1332.8, -230) * mm, "end": v(-1329.8, -230) * mm});
            skLineSegment(sketch, "E75.left", {"start": v(-1332.8, -30) * mm, "end": v(-1332.8, -230) * mm});
            skLineSegment(sketch, "E75.right", {"start": v(-1329.8, -30) * mm, "end": v(-1329.8, -224) * mm});
            skLineSegment(sketch, "E76.bottom", {"start": v(-1329.8, -230) * mm, "end": v(-1135.8, -230) * mm});
            skLineSegment(sketch, "E76.top", {"start": v(-1329.8, -224) * mm, "end": v(-1135.8, -224) * mm});
            skLineSegment(sketch, "E77.bottom", {"start": v(-1135.8, -230) * mm, "end": v(-1132.8, -230) * mm});
            skLineSegment(sketch, "E77.top", {"start": v(-1135.8, -30) * mm, "end": v(-1132.8, -30) * mm});
            skLineSegment(sketch, "E77.left", {"start": v(-1135.8, -224) * mm, "end": v(-1135.8, -30) * mm});
            skLineSegment(sketch, "E77.right", {"start": v(-1132.8, -230) * mm, "end": v(-1132.8, -30) * mm});
            skSolve(sketch);
        }
        {
            var Q0;
            Q0=qSketchRegion(id+"F48",true);
            extrude(context, id + "F49", {"entities" : qUnion([Q0]), "operationType" : NewBodyOperationType.ADD, "depth" : 40 * mm});
        }
        {
            var Q0;
            Q0=makeQuery(id+"F34.opExtrude","CAP_FACE",FACE,{"disambiguationData":[OSD([sQuery(id+"F33.wireOp",EDGE,"E36.MirrorCS"),sQuery(id+"F33.wireOp",EDGE,"E37.MirrorCS"),sQuery(id+"F33.wireOp",EDGE,"E39.MirrorCS"),sQuery(id+"F33.wireOp",EDGE,"E41.MirrorCS"),sQuery(id+"F33.wireOp",EDGE,"E42.MirrorCS"),sQuery(id+"F33.wireOp",EDGE,"E43.MirrorCS"),sQuery(id+"F33.wireOp",EDGE,"E44.MirrorC"),sQuery(id+"F33.wireOp",EDGE,"E45.MirrorC"),sQuery(id+"F33.wireOp",EDGE,"E46.MirrorCS"),sQuery(id+"F33.wireOp",EDGE,"E47.MirrorCS")])],"isStart":false});
            var sketch = newSketch(context, id + "F50", { "sketchPlane" : qUnion([Q0])});
            skArc(sketch, "E78", {"start": v(-0.8, 28) * mm, "mid": v(-28, -0.76) * mm, "end": v(0.73, -28) * mm});
            skLineSegment(sketch, "E79", {"start": v(-38.65, -10.5) * mm, "end": v(-68.65, -10.5) * mm});
            skLineSegment(sketch, "E80", {"start": v(-38.65, 10.5) * mm, "end": v(-68.65, 10.5) * mm});
            skLineSegment(sketch, "E81", {"start": v(-71.65, 13.5) * mm, "end": v(-71.65, 18.3) * mm});
            skLineSegment(sketch, "E82", {"start": v(-71.65, -13.5) * mm, "end": v(-71.65, -18.3) * mm});
            skLineSegment(sketch, "E83", {"start": v(-68.65, -21.3) * mm, "end": v(-33.65, -21.3) * mm});
            skLineSegment(sketch, "E84", {"start": v(-33.65, -21.3) * mm, "end": v(-12.38, -35.78) * mm});
            skLineSegment(sketch, "E85", {"start": v(-68.65, 21.3) * mm, "end": v(-33.29, 21.3) * mm});
            skLineSegment(sketch, "E86", {"start": v(-33.29, 21.3) * mm, "end": v(-12.75, 35.81) * mm});
            skLineSegment(sketch, "E87", {"start": v(-5.87, 34.74) * mm, "end": v(-0.8, 28) * mm});
            skLineSegment(sketch, "E88", {"start": v(-5.93, -35.07) * mm, "end": v(0.73, -28) * mm});
            skLineSegment(sketch, "E89", {"start": v(-33.65, 5.5) * mm, "end": v(-33.65, -5.5) * mm});
            skArc(sketch, "E90.filletArc", {"start": v(-33.65, 5.5) * mm, "mid": v(-35.12, 9.04) * mm, "end": v(-38.65, 10.5) * mm});
            skArc(sketch, "E91.filletArc", {"start": v(-38.65, -10.5) * mm, "mid": v(-35.12, -9.04) * mm, "end": v(-33.65, -5.5) * mm});
            skArc(sketch, "E92.filletArc", {"start": v(-5.87, 34.74) * mm, "mid": v(-9.1, 36.67) * mm, "end": v(-12.75, 35.81) * mm});
            skArc(sketch, "E93.filletArc", {"start": v(-12.38, -35.78) * mm, "mid": v(-9.02, -36.61) * mm, "end": v(-5.93, -35.07) * mm});
            skCircle(sketch, "E94", {"center": v(-62.9, -16) * mm, "radius": 2.93 * mm});
            skCircle(sketch, "E95", {"center": v(-63, 16) * mm, "radius": 3 * mm});
            skCircle(sketch, "E96", {"center": v(-55, 16) * mm, "radius": 2.81 * mm});
            skCircle(sketch, "E97", {"center": v(-55, -16) * mm, "radius": 2.69 * mm});
            skCircle(sketch, "E98", {"center": v(-63, 16) * mm, "radius": 2.74 * mm});
            skArc(sketch, "E99.filletArc", {"start": v(-68.65, 21.3) * mm, "mid": v(-70.78, 20.42) * mm, "end": v(-71.65, 18.3) * mm});
            skArc(sketch, "E100.filletArc", {"start": v(-71.65, 13.5) * mm, "mid": v(-70.78, 11.38) * mm, "end": v(-68.65, 10.5) * mm});
            skArc(sketch, "E101.filletArc", {"start": v(-68.65, -10.5) * mm, "mid": v(-70.78, -11.38) * mm, "end": v(-71.65, -13.5) * mm});
            skArc(sketch, "E102.filletArc", {"start": v(-71.65, -18.3) * mm, "mid": v(-70.78, -20.42) * mm, "end": v(-68.65, -21.3) * mm});
            skSolve(sketch);
        }
        {
            var Q0;
            Q0 = qSketchRegion(id + "F50", true);
            extrude(context, id + "F51", {"entities" : qUnion([Q0]), "depth" : 6 * mm});
        }
    });
